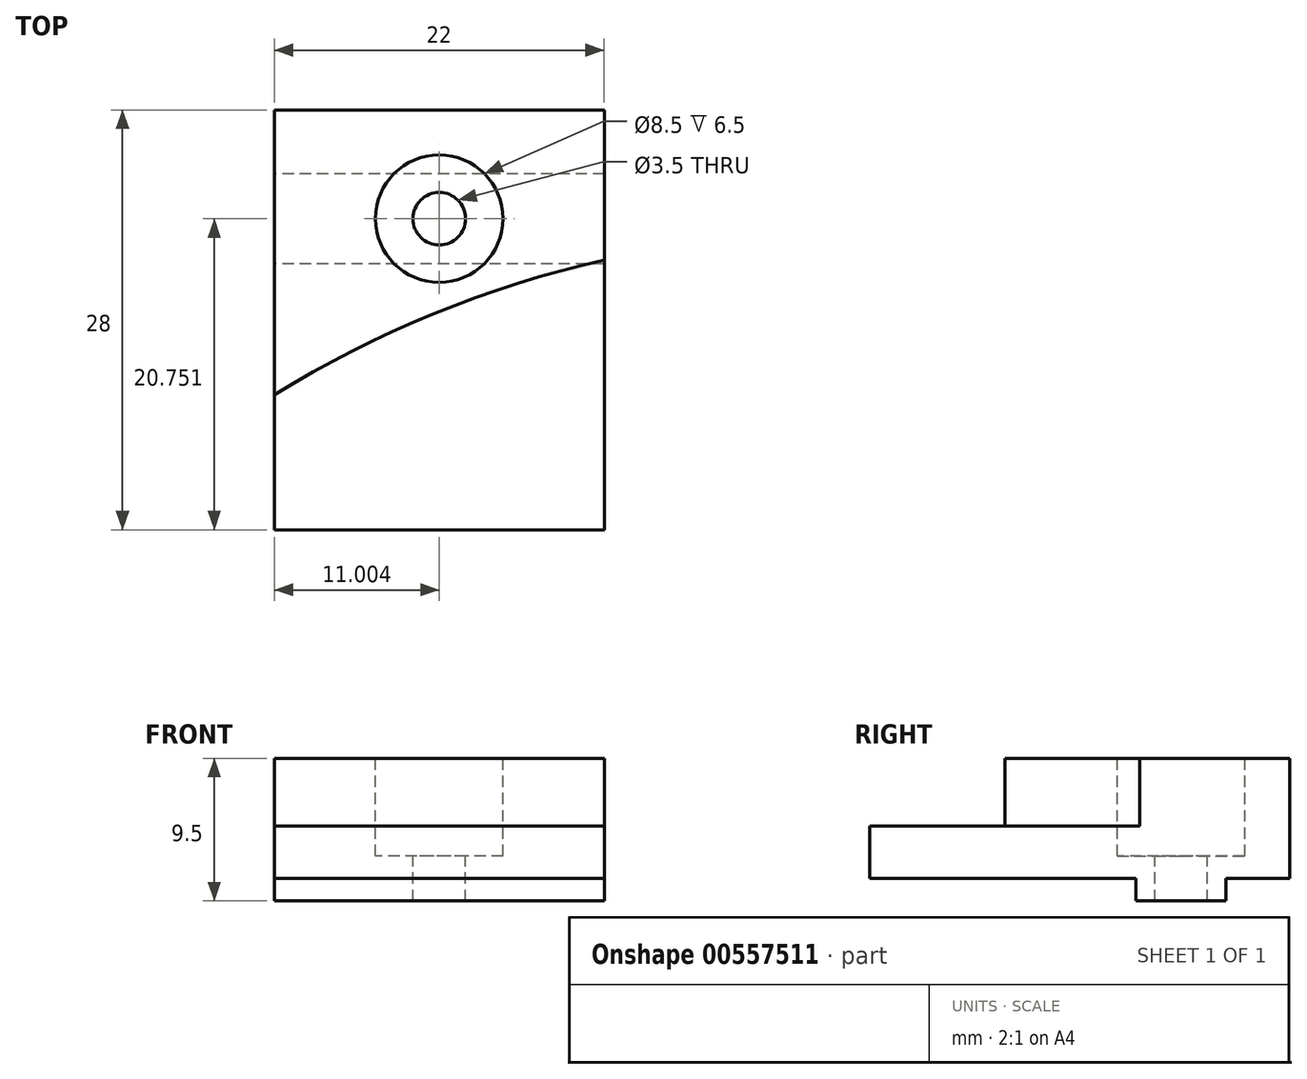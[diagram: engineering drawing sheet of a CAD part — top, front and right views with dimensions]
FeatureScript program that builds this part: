
annotation { "Feature Type Name" : "Feature", "Feature Type Description" : "" }
export const myFeature = defineFeature(function(context is Context, id is Id, definition is map)
    precondition{}
    {
        {
            var Q0;
            Q0=qCreatedBy(makeId("Top.planeOp"),FACE);
            var sketch = newSketch(context, id + "F0", { "sketchPlane" : qUnion([Q0])});
            skLineSegment(sketch, "E0.bottom", {"start": v(-9.19, 7.7) * mm, "end": v(12.81, 7.7) * mm});
            skLineSegment(sketch, "E0.top", {"start": v(-9.19, -20.3) * mm, "end": v(12.81, -20.3) * mm});
            skLineSegment(sketch, "E0.left", {"start": v(-9.19, 7.7) * mm, "end": v(-9.19, -20.3) * mm});
            skLineSegment(sketch, "E0.right", {"start": v(12.81, 7.7) * mm, "end": v(12.81, -20.3) * mm});
            skSolve(sketch);
        }
        {
            var Q0;
            Q0=makeQuery(id+"F0.imprint","IMPRINT",FACE,{"disambiguationData":[TD([[makeQuery(id+"F0.imprint","IMPRINT",EDGE,{"derivedFrom":sQuery(id+"F0.wireOp",EDGE,"E0.bottom")}),-1.0]])]});
            extrude(context, id + "F1", {"entities" : qUnion([Q0]), "depth" : 3.5 * mm, "offsetDistance" : 25 * mm});
        }
        {
            var Q0;
            Q0=makeQuery(id+"F1.opExtrude","CAP_FACE",FACE,{"disambiguationData":[OSD([sQuery(id+"F0.wireOp",EDGE,"E0.bottom"),sQuery(id+"F0.wireOp",EDGE,"E0.top"),sQuery(id+"F0.wireOp",EDGE,"E0.left"),sQuery(id+"F0.wireOp",EDGE,"E0.right")])],"isStart":false});
            var sketch = newSketch(context, id + "F2", { "sketchPlane" : qUnion([Q0])});
            skCircle(sketch, "E1", {"center": v(1.81, 0.45) * mm, "radius": 4.25 * mm});
            skPoint(sketch, "E1.centerSnap0", {"position": v(1.81, 7.7) * mm});
            skCircle(sketch, "E2", {"center": v(1.81, 0.45) * mm, "radius": 1.75 * mm});
            skPoint(sketch, "E3", {"position": v(12.81, -2.3) * mm});
            skPoint(sketch, "E4", {"position": v(-9.19, -11.3) * mm});
            skArc(sketch, "E5", {"start": v(12.81, -2.3) * mm, "mid": v(1.44, -5.9) * mm, "end": v(-9.19, -11.3) * mm});
            skSolve(sketch);
        }
        {
            var Q0;
            Q0=makeQuery(id+"F2.imprint","IMPRINT",FACE,{"disambiguationData":[TD([[makeQuery(id+"F2.imprint","IMPRINT",EDGE,{"derivedFrom":sQuery(id+"F2.wireOp",EDGE,"E1")}),1.0]])]});
            extrude(context, id + "F3", {"entities" : qUnion([Q0]), "operationType" : NewBodyOperationType.REMOVE, "oppositeDirection" : true, "depth" : 2 * mm, "offsetDistance" : 25 * mm});
        }
        {
            var Q0;
            Q0=makeQuery(id+"F3.boolean.opBoolean","SPLIT",FACE,{"disambiguationData":[TD([makeQuery(id+"F3.opExtrude","SWEPT_FACE",FACE,{"disambiguationData":[OSD([sQuery(id+"F2.wireOp",EDGE,"E2")])]})])],"derivedFrom":makeQuery(id+"F1.opExtrude","CAP_FACE",FACE,{"disambiguationData":[OSD([sQuery(id+"F0.wireOp",EDGE,"E0.bottom"),sQuery(id+"F0.wireOp",EDGE,"E0.top"),sQuery(id+"F0.wireOp",EDGE,"E0.left"),sQuery(id+"F0.wireOp",EDGE,"E0.right")])],"isStart":false})});
            extrude(context, id + "F4", {"entities" : qUnion([Q0]), "operationType" : NewBodyOperationType.REMOVE, "endBound" : BoundingType.THROUGH_ALL, "oppositeDirection" : true, "depth" : 25 * mm, "offsetDistance" : 25 * mm});
        }
        {
            var Q0;
            Q0=makeQuery(id+"F1.opExtrude","CAP_FACE",FACE,{"disambiguationData":[OSD([sQuery(id+"F0.wireOp",EDGE,"E0.bottom"),sQuery(id+"F0.wireOp",EDGE,"E0.top"),sQuery(id+"F0.wireOp",EDGE,"E0.left"),sQuery(id+"F0.wireOp",EDGE,"E0.right")])],"isStart":true});
            var sketch = newSketch(context, id + "F5", { "sketchPlane" : qUnion([Q0])});
            skLineSegment(sketch, "E6.bottom", {"start": v(12.81, -3.45) * mm, "end": v(-9.19, -3.45) * mm});
            skLineSegment(sketch, "E6.top", {"start": v(12.81, 2.55) * mm, "end": v(-9.19, 2.55) * mm});
            skLineSegment(sketch, "E6.left", {"start": v(12.81, -3.45) * mm, "end": v(12.81, 2.55) * mm});
            skLineSegment(sketch, "E6.right", {"start": v(-9.19, -3.45) * mm, "end": v(-9.19, 2.55) * mm});
            skPoint(sketch, "E6.middle", {"position": v(1.81, -0.45) * mm});
            skSolve(sketch);
        }
        {
            var Q0;
            Q0=makeQuery(id+"F5.imprint","IMPRINT",FACE,{"disambiguationData":[TD([[makeQuery(id+"F5.imprint","IMPRINT",EDGE,{"derivedFrom":sQuery(id+"F5.wireOp",EDGE,"E6.bottom")}),-1.0]])]});
            extrude(context, id + "F6", {"entities" : qUnion([Q0]), "operationType" : NewBodyOperationType.ADD, "depth" : 1.5 * mm, "offsetDistance" : 25 * mm});
        }
        {
            var Q0;
            Q0=makeQuery(id+"F2.imprint","IMPRINT",FACE,{"disambiguationData":[TD([[makeQuery(id+"F2.imprint","IMPRINT",EDGE,{"derivedFrom":sQuery(id+"F2.wireOp",EDGE,"E1")}),-1.0]])]});
            extrude(context, id + "F7", {"entities" : qUnion([Q0]), "operationType" : NewBodyOperationType.ADD, "depth" : 4.5 * mm, "offsetDistance" : 25 * mm});
        }
    });
